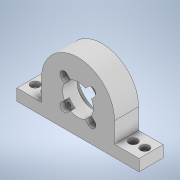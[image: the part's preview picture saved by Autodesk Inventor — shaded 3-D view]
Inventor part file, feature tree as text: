
AUTODESK INVENTOR PART (.ipt)
format: ipt  version: 2020 (Build 240168000, 168)  size: 257,024 bytes
history: native  units: mm
features: other x8, sketch x5, reference x4, extrude x3, hole x2, projected_geometry x1
ambient origin geometry x8: Origin, YZ Plane, XZ Plane, XY Plane, X Axis, Y Axis, Z Axis, Center Point
bodies: Body1 (feature_tree)
feature tree (23):
  other  "솔리드1"
  other  "작업 평면1"
  extrude  "돌출1"  Depth=12.0mm
  extrude  "돌출3"  Depth=15.0mm TaperAngle=0.0deg
  hole  "구멍3"  [1 undecoded]
  extrude  "돌출4"  Depth=127.0mm
  hole  "구멍5"  [1 undecoded]
  sketch  "스케치1"
  reference  "참조1"
  reference  "참조6"
  reference  "참조10"
  sketch  "스케치5"
  reference  "참조15"
  sketch  "스케치9"
  sketch  "스케치11"
  sketch  "스케치12"
  projected_geometry  "투영된 루프8"
  other  "<userpath>\Documents\Inventor\CoMoVi\조립품3.iam"
  other  "조립품3.iam"
  other  "Motor:1"
  other  "bearing:1"
  other  "<userpath>\Documents\Inventor\CoMoVi\조립품1.iam"
  other  "조립품1.iam"
note: 2 required parameter values undecoded (feature->parameter linkage not recoverable at this tier; creation-order binding heuristic only, values carry confidence <= 0.55)
